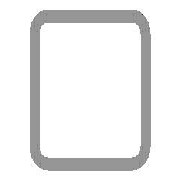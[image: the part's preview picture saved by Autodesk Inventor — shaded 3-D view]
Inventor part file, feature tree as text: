
AUTODESK INVENTOR PART (.ipt)
format: ipt  version: 2025 (Build 290162010, 162A)  size: 148,992 bytes
history: native  units: mm (DEFAULTED — no unit token found)
features: other x3, sketch x1, plane x1
ambient origin geometry x8: Origin, YZ Plane, XZ Plane, XY Plane, X Axis, Y Axis, Z Axis, Center Point
bodies: Solid1 (feature_tree), Body (feature_tree)
feature tree (5):
  other  "Driven Length"
  other  "Start plane"
  other  "End plane"
  sketch  "Sketch3"  dims[d3=2200.0mm d4=0.0mm d7=6.0mm d9=50.0mm d11=100.0mm d12=3.0mm d13=-0.0mm d14=8200.0mm d15=25.0mm d16=50.0mm d17=90.0deg d18=8200.0mm]
  plane  "Work Plane3"
